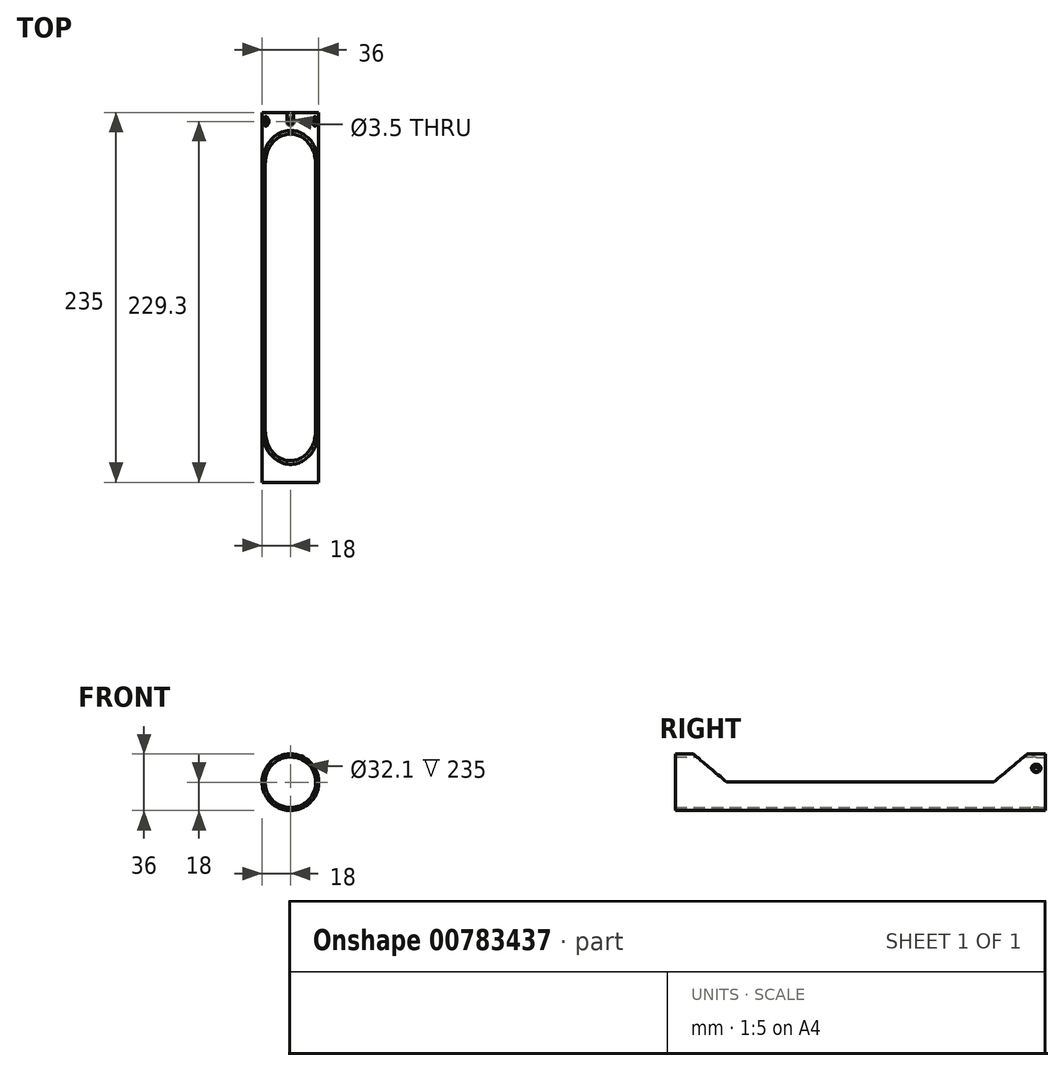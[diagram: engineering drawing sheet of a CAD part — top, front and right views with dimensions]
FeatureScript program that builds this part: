
annotation { "Feature Type Name" : "Feature", "Feature Type Description" : "" }
export const myFeature = defineFeature(function(context is Context, id is Id, definition is map)
    precondition{}
    {
        {
            var Q0;
            Q0=qCreatedBy(makeId("Front.planeOp"),FACE);
            var sketch = newSketch(context, id + "F0", { "sketchPlane" : qUnion([Q0])});
            skCircle(sketch, "E0", {"center": v(0, 0) * mm, "radius": 18 * mm});
            skCircle(sketch, "E1", {"center": v(0, 0) * mm, "radius": 16.05 * mm});
            skLineSegment(sketch, "E2.bottom", {"start": v(18, -18) * mm, "end": v(-18, -18) * mm});
            skLineSegment(sketch, "E2.top", {"start": v(18, 18) * mm, "end": v(-18, 18) * mm});
            skLineSegment(sketch, "E2.left", {"start": v(18, -18) * mm, "end": v(18, 18) * mm});
            skLineSegment(sketch, "E2.right", {"start": v(-18, -18) * mm, "end": v(-18, 18) * mm});
            skLineSegment(sketch, "E3", {"start": v(0, 0) * mm, "end": v(0, 18) * mm});
            skLineSegment(sketch, "E4", {"start": v(0, 0) * mm, "end": v(0, -18) * mm});
            skLineSegment(sketch, "E5", {"start": v(0, 0) * mm, "end": v(-15.59, 9) * mm});
            skLineSegment(sketch, "E6", {"start": v(0, 0) * mm, "end": v(15.59, 9) * mm});
            skSolve(sketch);
        }
        {
            var Q0;
            {var subQ3=sQuery(id+"F0.wireOp",EDGE,"CAZaTLFN-tJie-LHG7-8vTy-squ8jarRoMMn");var subQ5=sQuery(id+"F0.wireOp",EDGE,"E1");var subQ6=makeQuery(id+"F0.imprint","INTERSECT",VERTEX,{"derivedFrom":[subQ5,subQ3]});Q0=makeQuery(id+"F0.imprint","IMPRINT",FACE,{"disambiguationData":[TD([[makeQuery(id+"F0.imprint","IMPRINT",EDGE,{"disambiguationData":[TD([[subQ6,1.0]])],"derivedFrom":subQ5}),-1.0]])]});}
            var Q1;
            {var subQ3=sQuery(id+"F0.wireOp",EDGE,"CAZaTLFN-tJie-LHG7-8vTy-squ8jarRoMMn");var subQ5=sQuery(id+"F0.wireOp",EDGE,"E1");var subQ6=makeQuery(id+"F0.imprint","INTERSECT",VERTEX,{"derivedFrom":[subQ5,subQ3]});Q1=makeQuery(id+"F0.imprint","IMPRINT",FACE,{"disambiguationData":[TD([[makeQuery(id+"F0.imprint","IMPRINT",EDGE,{"disambiguationData":[TD([[subQ6,-1.0]])],"derivedFrom":subQ5}),-1.0]])]});}
            var Q2;
            {var subQ0=sQuery(id+"F0.wireOp",EDGE,"l8s0sOfb-fzFU-R0BE-n0NO-c75pVUIZOnGM");var subQ1=sQuery(id+"F0.wireOp",EDGE,"E0");var subQ2=makeQuery(id+"F0.imprint","INTERSECT",VERTEX,{"derivedFrom":[subQ1,subQ0]});Q2=makeQuery(id+"F0.imprint","IMPRINT",FACE,{"disambiguationData":[TD([[makeQuery(id+"F0.imprint","IMPRINT",EDGE,{"disambiguationData":[TD([[subQ2,1.0]])],"derivedFrom":subQ1}),1.0]])]});}
            var Q3;
            {var subQ0=sQuery(id+"F0.wireOp",EDGE,"4xxhsBqu-Dr4I-gKWc-ZI2R-gIkBFB4eemaq");var subQ1=sQuery(id+"F0.wireOp",EDGE,"E0");var subQ2=makeQuery(id+"F0.imprint","INTERSECT",VERTEX,{"derivedFrom":[subQ1,subQ0]});Q3=makeQuery(id+"F0.imprint","IMPRINT",FACE,{"disambiguationData":[TD([[makeQuery(id+"F0.imprint","IMPRINT",EDGE,{"disambiguationData":[TD([[subQ2,-1.0]])],"derivedFrom":subQ1}),1.0]])]});}
            var Q4;
            Q4=sQuery(id+"F0.wireOp",EDGE,"E0");
            extrude(context, id + "F1", {"entities" : qUnion([Q0, Q1, Q2, Q3]), "surfaceEntities" : qUnion([Q4]), "depth" : 117.5 * mm, "offsetDistance" : 25.4 * mm, "hasSecondDirection" : true, "secondDirectionOppositeDirection" : true, "secondDirectionDepth" : 117.5 * mm});
        }
        {
            var Q0;
            Q0=qCreatedBy(makeId("Right.planeOp"),FACE);
            var sketch = newSketch(context, id + "F2", { "sketchPlane" : qUnion([Q0])});
            skLineSegment(sketch, "E7.bottom", {"start": v(106.1, 0.2) * mm, "end": v(-106.1, 0.2) * mm});
            skLineSegment(sketch, "E7.top", {"start": v(106.1, 35.8) * mm, "end": v(-106.1, 35.8) * mm});
            skLineSegment(sketch, "E7.left", {"start": v(106.1, 0.2) * mm, "end": v(106.1, 35.8) * mm});
            skLineSegment(sketch, "E7.right", {"start": v(-106.1, 0.2) * mm, "end": v(-106.1, 35.8) * mm});
            skPoint(sketch, "E7.middle", {"position": v(0, 18) * mm});
            skLineSegment(sketch, "E8", {"start": v(-117.5, 18) * mm, "end": v(117.5, 18) * mm});
            skLineSegment(sketch, "E9", {"start": v(117.5, -18) * mm, "end": v(-117.5, -18) * mm});
            skLineSegment(sketch, "E10", {"start": v(106.1, 18) * mm, "end": v(84.89, 0.2) * mm});
            skLineSegment(sketch, "E11.MirrorCS", {"start": v(-106.1, 18) * mm, "end": v(-84.89, 0.2) * mm});
            skSolve(sketch);
        }
        {
            var Q0;
            {var subQ0=sQuery(id+"F2.wireOp",EDGE,"E7.top");Q0=makeQuery(id+"F2.imprint","IMPRINT",FACE,{"disambiguationData":[TD([[makeQuery(id+"F2.imprint","IMPRINT",EDGE,{"derivedFrom":subQ0}),1.0]])]});}
            var Q1;
            {var subQ0=sQuery(id+"F2.wireOp",EDGE,"E10");Q1=makeQuery(id+"F2.imprint","IMPRINT",FACE,{"disambiguationData":[TD([[makeQuery(id+"F2.imprint","IMPRINT",EDGE,{"derivedFrom":subQ0}),-1.0]])]});}
            extrude(context, id + "F3", {"entities" : qUnion([Q0, Q1]), "operationType" : NewBodyOperationType.REMOVE, "oppositeDirection" : true, "depth" : 50.8 * mm, "offsetDistance" : 25.4 * mm, "hasSecondDirection" : true, "secondDirectionOppositeDirection" : false, "secondDirectionDepth" : 50.8 * mm});
        }
        {
            var Q0;
            Q0=sQuery(id+"F0.wireOp",VERTEX,"E5.end");
            var Q1;
            Q1=sQuery(id+"F0.wireOp",EDGE,"E5");
            cPlane(context, id + "F4", {"entities" : qUnion([Q0, Q1]), "cplaneType" : CPlaneType.CURVE_POINT, "offset" : 25 * mm, "width" : 150 * mm, "height" : 150 * mm});
        }
        {
            var Q0;
            Q0=qCreatedBy(id+"F4.planeOp",FACE);
            var sketch = newSketch(context, id + "F5", { "sketchPlane" : qUnion([Q0])});
            skPoint(sketch, "E12", {"position": v(-111.8, 0) * mm});
            skPoint(sketch, "E13.MirrorP", {"position": v(111.8, 0) * mm});
            skSolve(sketch);
        }
        {
            var Q0;
            Q0=sQuery(id+"F5.wireOp",VERTEX,"E12");
            var Q1;
            Q1=makeQuery(id+"F1.opExtrude","SWEPT_BODY",BODY,{"disambiguationData":[OSD([sQuery(id+"F0.wireOp",EDGE,"E0"),sQuery(id+"F0.wireOp",EDGE,"E1")])]});
            hole(context, id + "F6", {"style" : HoleStyle.C_SINK, "endStyle" : HoleEndStyle.BLIND, "holeDiameter" : 3.5 * mm, "cSinkDiameter" : 6 * mm, "cSinkAngle" : 100 * degree, "majorDiameter" : 5 * mm, "holeDepth" : 5 * mm, "isTappedThrough" : true, "tappedDepth" : 12 * mm, "tapClearance" : 3, "locations" : qUnion([Q0]), "scope" : qUnion([Q1])});
        }
        {
            var Q0;
            Q0=sQuery(id+"F0.wireOp",VERTEX,"E6.end");
            var Q1;
            Q1=sQuery(id+"F0.wireOp",EDGE,"E6");
            cPlane(context, id + "F7", {"entities" : qUnion([Q0, Q1]), "cplaneType" : CPlaneType.CURVE_POINT, "offset" : 25 * mm, "width" : 150 * mm, "height" : 150 * mm});
        }
        {
            var Q0;
            Q0=qCreatedBy(id+"F7.planeOp",FACE);
            var sketch = newSketch(context, id + "F8", { "sketchPlane" : qUnion([Q0])});
            skPoint(sketch, "E14", {"position": v(111.8, 0) * mm});
            skSolve(sketch);
        }
        {
            var Q0;
            Q0=sQuery(id+"F8.wireOp",VERTEX,"E14");
            var Q1;
            Q1=makeQuery(id+"F1.opExtrude","SWEPT_BODY",BODY,{"disambiguationData":[OSD([sQuery(id+"F0.wireOp",EDGE,"E0"),sQuery(id+"F0.wireOp",EDGE,"E1")])]});
            hole(context, id + "F9", {"style" : HoleStyle.C_SINK, "endStyle" : HoleEndStyle.BLIND, "holeDiameter" : 3.5 * mm, "cSinkDiameter" : 6 * mm, "cSinkAngle" : 100 * degree, "majorDiameter" : 5 * mm, "holeDepth" : 5 * mm, "isTappedThrough" : true, "tappedDepth" : 12 * mm, "tapClearance" : 3, "locations" : qUnion([Q0]), "scope" : qUnion([Q1])});
        }
        {
            var Q0;
            Q0=sQuery(id+"F0.wireOp",VERTEX,"E3.end");
            var Q1;
            Q1=sQuery(id+"F0.wireOp",EDGE,"E3");
            cPlane(context, id + "F10", {"entities" : qUnion([Q0, Q1]), "cplaneType" : CPlaneType.CURVE_POINT, "offset" : 25 * mm, "width" : 150 * mm, "height" : 150 * mm});
        }
        {
            var Q0;
            Q0=qCreatedBy(id+"F10.planeOp",FACE);
            var sketch = newSketch(context, id + "F11", { "sketchPlane" : qUnion([Q0])});
            skCircle(sketch, "E15", {"center": v(0, 111.8) * mm, "radius": 2 * mm});
            skLineSegment(sketch, "E16", {"start": v(2, 111.8) * mm, "end": v(2, 117.5) * mm});
            skLineSegment(sketch, "E17", {"start": v(-2, 111.8) * mm, "end": v(-2, 117.5) * mm});
            skLineSegment(sketch, "E18", {"start": v(-2, 117.5) * mm, "end": v(2, 117.5) * mm});
            skLineSegment(sketch, "E19.0", {"start": v(18, 117.5) * mm, "end": v(-18, 117.5) * mm});
            skSolve(sketch);
        }
        {
            var Q0;
            {var subQ0=sQuery(id+"F11.wireOp",EDGE,"E16");Q0=makeQuery(id+"F11.imprint","IMPRINT",FACE,{"disambiguationData":[TD([[makeQuery(id+"F11.imprint","IMPRINT",EDGE,{"derivedFrom":subQ0}),1.0]])]});}
            var Q1;
            {var subQ0=sQuery(id+"F11.wireOp",EDGE,"E15");var subQ1=makeQuery(id+"F11.imprint","INTERSECT",VERTEX,{"derivedFrom":[subQ0,sQuery(id+"F11.wireOp",EDGE,"E16")]});Q1=makeQuery(id+"F11.imprint","IMPRINT",FACE,{"disambiguationData":[TD([[makeQuery(id+"F11.imprint","IMPRINT",EDGE,{"disambiguationData":[TD([[subQ1,-1.0]])],"derivedFrom":subQ0}),1.0]])]});}
            extrude(context, id + "F12", {"entities" : qUnion([Q0, Q1]), "operationType" : NewBodyOperationType.REMOVE, "oppositeDirection" : true, "depth" : 19.1 * mm, "offsetDistance" : 25 * mm});
        }
        {
            var Q0;
            Q0=sQuery(id+"F0.wireOp",EDGE,"E2.bottom");
            cPoint(context, id + "F13", {"entities" : qUnion([Q0]), "parameter" : 0.5});
        }
        {
            var Q0;
            Q0=qCreatedBy(id+"F13",VERTEX);
            var Q1;
            Q1=sQuery(id+"F0.wireOp",EDGE,"E4");
            cPlane(context, id + "F14", {"entities" : qUnion([Q0, Q1]), "cplaneType" : CPlaneType.CURVE_POINT, "offset" : 25 * mm, "width" : 150 * mm, "height" : 150 * mm});
        }
        {
            var Q0;
            Q0=qCreatedBy(id+"F14.planeOp",FACE);
            var sketch = newSketch(context, id + "F15", { "sketchPlane" : qUnion([Q0])});
            skPoint(sketch, "E20", {"position": v(0, -111.8) * mm});
            skSolve(sketch);
        }
        {
            var Q0;
            Q0=sQuery(id+"F15.wireOp",VERTEX,"E20");
            var Q1;
            Q1=makeQuery(id+"F1.opExtrude","SWEPT_BODY",BODY,{"disambiguationData":[OSD([sQuery(id+"F0.wireOp",EDGE,"E0"),sQuery(id+"F0.wireOp",EDGE,"E1")])]});
            hole(context, id + "F16", {"style" : HoleStyle.C_SINK, "endStyle" : HoleEndStyle.BLIND, "holeDiameter" : 3.5 * mm, "cSinkDiameter" : 6 * mm, "cSinkAngle" : 100 * degree, "majorDiameter" : 5 * mm, "holeDepth" : 5 * mm, "isTappedThrough" : true, "tappedDepth" : 12 * mm, "tapClearance" : 3, "locations" : qUnion([Q0]), "scope" : qUnion([Q1])});
        }
    });
